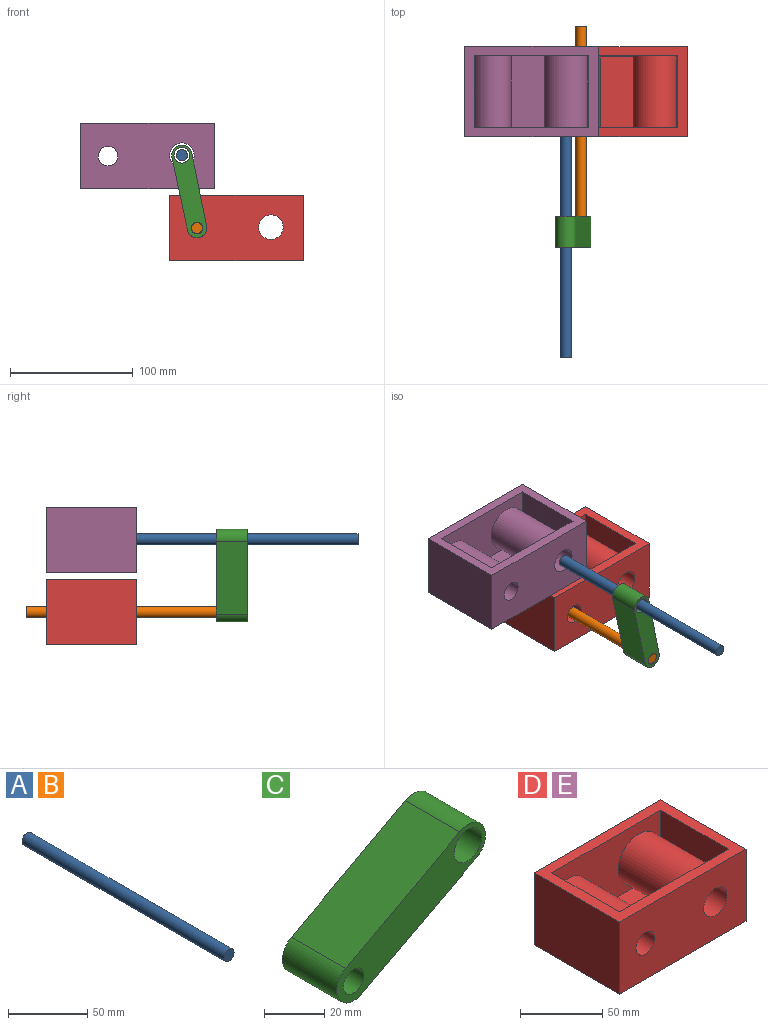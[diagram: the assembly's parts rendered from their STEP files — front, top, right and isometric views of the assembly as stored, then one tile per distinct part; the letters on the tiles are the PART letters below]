
ASSEMBLY  parts=5 mates=4
PART A: 3 faces, bbox 9x180.3x9 mm
  f0: cylinder r=4.49mm len=180.34mm, axis (0,1,0), area 5086.3mm2, adj f1,f2
  f1: plane 8.98x8.98mm, normal (0,-1,0), area 63.3mm2, adj f0
  f2: plane 8.98x8.98mm, normal (0,1,0), area 63.3mm2, adj f0
PART B: same geometry as A
PART C: 8 faces, bbox 69.7x25.4x44.6 mm
  f0: plane 53.39x28.67mm, normal (-0.47,0,0.88), area 1539.2mm2, adj f1,f4,f6,f7
  f1: cylinder r=7.96mm len=25.4mm, axis (0,1,0), area 627.2mm2, adj f0,f2,f6,f7
  f2: plane 54.05x28.34mm, normal (0.46,0,-0.89), area 1550.1mm2, adj f1,f4,f6,f7
  f3: cylinder r=4.8mm len=25.4mm, axis (0,1,0), area 766.5mm2, adj f6,f7
  f4: cylinder r=8.26mm len=25.4mm, axis (0,1,0), area 656.3mm2, adj f0,f2,f6,f7
  f5: cylinder r=6.42mm len=25.4mm, axis (0,1,0), area 1025.1mm2, adj f6,f7
  f6: plane 69.75x44.63mm, normal (0,-1,0), area 987.3mm2, adj f0,f1,f2,f3,f4,f5
  f7: plane 69.75x44.63mm, normal (0,1,0), area 987.3mm2, adj f0,f1,f2,f3,f4,f5
PART D: 16 faces, bbox 108.7x73.4x53.6 mm
  f0: plane 108.66x73.41mm, normal (0,0,1), area 2542.5mm2, adj f1,f3,f6,f7,f9,f11,f14,f15
  f1: plane 73.41x53.56mm, normal (-1,0,0), area 3931.9mm2, adj f0,f2,f6,f7
  f2: plane 108.66x73.41mm, normal (0,0,-1), area 7976.5mm2, adj f1,f3,f6,f7
  f3: plane 73.41x53.56mm, normal (1,0,0), area 3931.9mm2, adj f0,f2,f6,f7
  f4: cylinder r=8.01mm len=73.41mm, axis (0,-1,0), area 3694.9mm2, adj f6,f7
  f5: cylinder r=10mm len=73.41mm, axis (0,-1,0), area 4612.4mm2, adj f6,f7
  f6: plane 108.66x53.56mm, normal (0,1,0), area 5304.6mm2, adj f0,f1,f2,f3,f4,f5
  f7: plane 108.66x53.56mm, normal (0,-1,0), area 5304.6mm2, adj f0,f1,f2,f3,f4,f5
  f8: plane 58.17x13.48mm, normal (1,0,0), area 784.3mm2, adj f10,f12,f14,f15
  f9: plane 58.17x21.16mm, normal (1,0,0), area 1230.9mm2, adj f0,f12,f14,f15
  f10: plane 93.42x58.17mm, normal (0,0,1), area 5434.1mm2, adj f8,f11,f14,f15
  f11: plane 58.17x45.94mm, normal (-1,0,0), area 2672.3mm2, adj f0,f10,f14,f15
  f12: cylinder r=15.63mm len=58.17mm, axis (0,-1,0), area 5040.4mm2, adj f8,f9,f14,f15
  f13: cylinder r=17.62mm len=58.17mm, axis (0,-1,0), area 6439.7mm2, adj f14,f15
  f14: plane 93.42x45.94mm, normal (0,-1,0), area 2557.2mm2, adj f0,f8,f9,f10,f11,f12,f13
  f15: plane 93.42x45.94mm, normal (0,1,0), area 2557.2mm2, adj f0,f8,f9,f10,f11,f12,f13
PART E: same geometry as D
PLACE A rot(axis=(0,1,0),120deg) t=(-73.12,0,72.66)mm
PLACE B rot(axis=(0,1,0),20deg) t=(47.02,90.17,-17.59)mm
PLACE C rot(axis=(0,-1,0),73.8deg) t=(-32.48,-64.77,110.31)mm
PLACE D t=(-16.07,0,16.33)mm fixed
PLACE E t=(-88.59,0,74.93)mm
MATE revolute E.f5 <-> A.f0  axis (0,-1,0) through (-6.26,0,102.4)mm
MATE revolute B.f0 <-> D.f4  axis (0,1,0) through (6.12,0,43.08)mm
MATE revolute A.f0 <-> C.f4  axis (0,1,0) through (-6.26,-90.17,102.4)mm
MATE revolute C.f1 <-> B.f0  axis (0,-1,0) through (6.12,-90.17,43.08)mm
